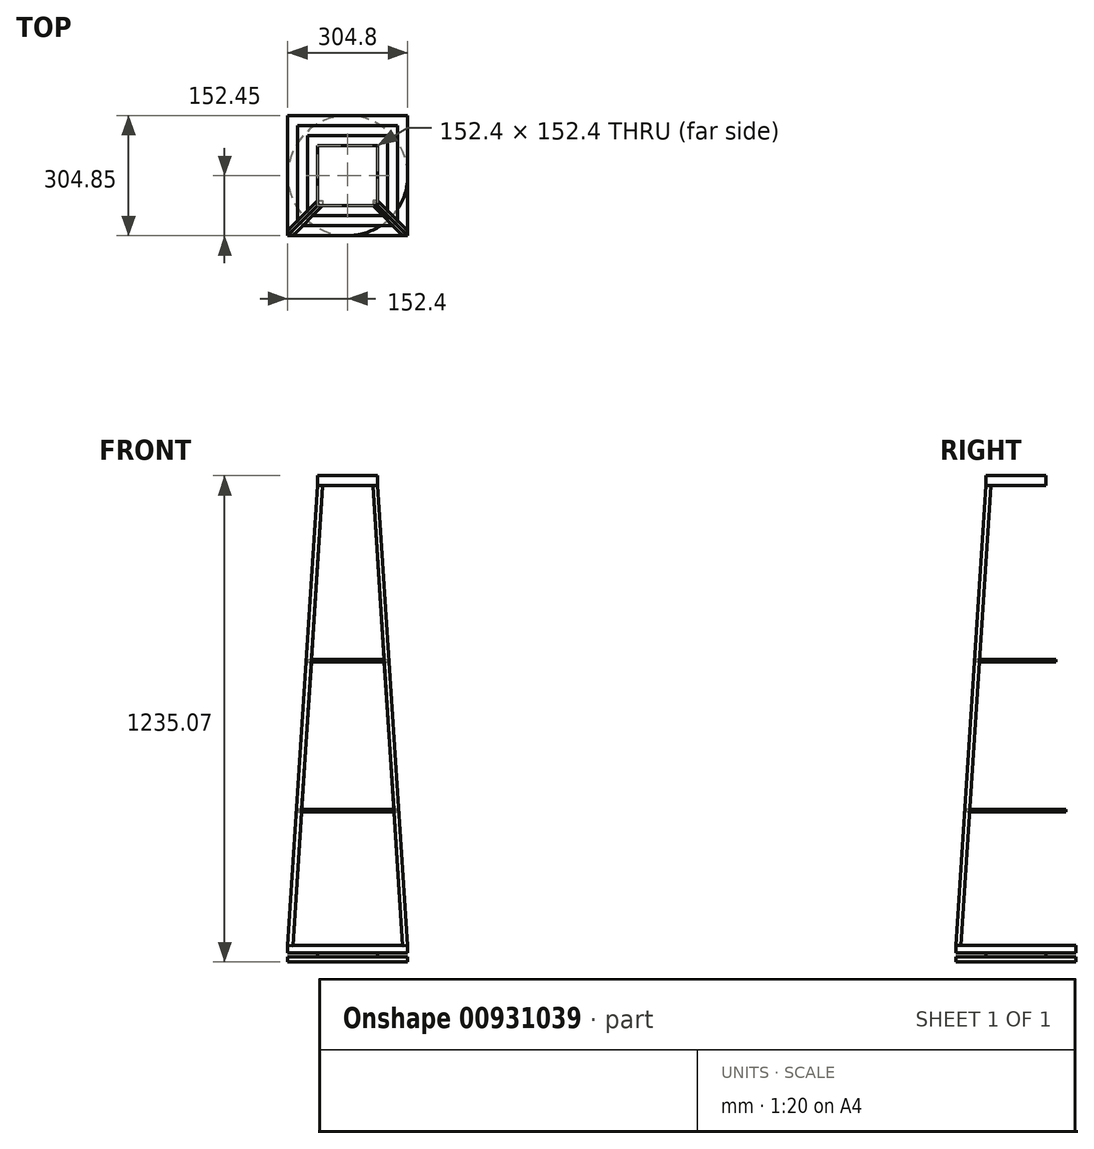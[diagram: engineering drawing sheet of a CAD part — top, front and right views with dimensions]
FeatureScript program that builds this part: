
annotation { "Feature Type Name" : "Feature", "Feature Type Description" : "" }
export const myFeature = defineFeature(function(context is Context, id is Id, definition is map)
    precondition{}
    {
        {
            var Q0;
            Q0=qCreatedBy(makeId("Top.planeOp"),FACE);
            var sketch = newSketch(context, id + "F0", { "sketchPlane" : qUnion([Q0])});
            skCircle(sketch, "E0", {"center": v(0, 0) * mm, "radius": 152.4 * mm});
            skSolve(sketch);
        }
        {
            var Q0;
            Q0 = qSketchRegion(id + "F0", true);
            extrude(context, id + "F1", {"entities" : qUnion([Q0]), "depth" : 12.7 * mm, "offsetDistance" : 25.4 * mm});
        }
        {
            var Q0;
            Q0=makeQuery(id+"F1.opExtrude","CAP_FACE",FACE,{"disambiguationData":[OSD([sQuery(id+"F0.wireOp",EDGE,"E0")])],"isStart":false});
            var sketch = newSketch(context, id + "F2", { "sketchPlane" : qUnion([Q0])});
            skLineSegment(sketch, "E1.bottom", {"start": v(76.2, 76.2) * mm, "end": v(-76.2, 76.2) * mm});
            skLineSegment(sketch, "E1.top", {"start": v(76.2, -76.2) * mm, "end": v(-76.2, -76.2) * mm});
            skLineSegment(sketch, "E1.left", {"start": v(76.2, 76.2) * mm, "end": v(76.2, -76.2) * mm});
            skLineSegment(sketch, "E1.right", {"start": v(-76.2, 76.2) * mm, "end": v(-76.2, -76.2) * mm});
            skPoint(sketch, "E1.middle", {"position": v(0, 0) * mm});
            skSolve(sketch);
        }
        {
            var Q0;
            Q0 = qSketchRegion(id + "F2", true);
            extrude(context, id + "F3", {"entities" : qUnion([Q0]), "operationType" : NewBodyOperationType.ADD, "depth" : 9.52 * mm, "offsetDistance" : 25.4 * mm});
        }
        {
            var Q0;
            Q0=makeQuery(id+"F3.opExtrude","CAP_FACE",FACE,{"disambiguationData":[OSD([sQuery(id+"F2.wireOp",EDGE,"E1.bottom"),sQuery(id+"F2.wireOp",EDGE,"E1.top"),sQuery(id+"F2.wireOp",EDGE,"E1.left"),sQuery(id+"F2.wireOp",EDGE,"E1.right")])],"isStart":false});
            var sketch = newSketch(context, id + "F4", { "sketchPlane" : qUnion([Q0])});
            skLineSegment(sketch, "E2.bottom", {"start": v(152.4, -152.4) * mm, "end": v(-152.4, -152.4) * mm});
            skLineSegment(sketch, "E2.top", {"start": v(152.4, 152.4) * mm, "end": v(-152.4, 152.4) * mm});
            skLineSegment(sketch, "E2.left", {"start": v(152.4, -152.4) * mm, "end": v(152.4, 152.4) * mm});
            skLineSegment(sketch, "E2.right", {"start": v(-152.4, -152.4) * mm, "end": v(-152.4, 152.4) * mm});
            skPoint(sketch, "E2.middle", {"position": v(0, 0) * mm});
            skSolve(sketch);
        }
        {
            var Q0;
            Q0 = qSketchRegion(id + "F4", true);
            extrude(context, id + "F5", {"entities" : qUnion([Q0]), "operationType" : NewBodyOperationType.ADD, "depth" : 19.05 * mm, "offsetDistance" : 25.4 * mm});
        }
        {
            var Q0;
            Q0=makeQuery(id+"F5.opExtrude","CAP_FACE",FACE,{"disambiguationData":[OSD([sQuery(id+"F4.wireOp",EDGE,"E2.bottom"),sQuery(id+"F4.wireOp",EDGE,"E2.top"),sQuery(id+"F4.wireOp",EDGE,"E2.left"),sQuery(id+"F4.wireOp",EDGE,"E2.right")])],"isStart":false});
            cPlane(context, id + "F6", {"entities" : qUnion([Q0]), "cplaneType" : CPlaneType.OFFSET, "offset" : 1168.4 * mm, "width" : 152.4 * mm, "height" : 152.4 * mm});
        }
        {
            var Q0;
            Q0=qCreatedBy(id+"F6.planeOp",FACE);
            var sketch = newSketch(context, id + "F7", { "sketchPlane" : qUnion([Q0])});
            skLineSegment(sketch, "E3.bottom", {"start": v(76.2, -76.2) * mm, "end": v(-76.2, -76.2) * mm});
            skLineSegment(sketch, "E3.top", {"start": v(76.2, 76.2) * mm, "end": v(-76.2, 76.2) * mm});
            skLineSegment(sketch, "E3.left", {"start": v(76.2, -76.2) * mm, "end": v(76.2, 76.2) * mm});
            skLineSegment(sketch, "E3.right", {"start": v(-76.2, -76.2) * mm, "end": v(-76.2, 76.2) * mm});
            skPoint(sketch, "E3.middle", {"position": v(0, 0) * mm});
            skSolve(sketch);
        }
        {
            var Q0;
            Q0 = qSketchRegion(id + "F7", true);
            extrude(context, id + "F8", {"entities" : qUnion([Q0]), "depth" : 25.4 * mm, "offsetDistance" : 25.4 * mm});
        }
        {
            var Q0;
            Q0=makeQuery(id+"F5.opExtrude","CAP_VERTEX",VERTEX,{"disambiguationData":[OSD([sQuery(id+"F4.wireOp",EDGE,"E2.bottom"),sQuery(id+"F4.wireOp",EDGE,"E2.right")])],"isStart":false});
            var Q1;
            Q1=makeQuery(id+"F5.opExtrude","CAP_VERTEX",VERTEX,{"disambiguationData":[OSD([sQuery(id+"F4.wireOp",EDGE,"E2.bottom"),sQuery(id+"F4.wireOp",EDGE,"E2.left")])],"isStart":false});
            var Q2;
            Q2=makeQuery(id+"F8.opExtrude","CAP_VERTEX",VERTEX,{"disambiguationData":[OSD([sQuery(id+"F7.wireOp",EDGE,"E3.bottom"),sQuery(id+"F7.wireOp",EDGE,"E3.right")])],"isStart":true});
            cPlane(context, id + "F9", {"entities" : qUnion([Q0, Q1, Q2]), "cplaneType" : CPlaneType.THREE_POINT, "offset" : 25.4 * mm, "width" : 152.4 * mm, "height" : 152.4 * mm});
        }
        {
            var Q0;
            Q0=qCreatedBy(id+"F9.planeOp",FACE);
            var sketch = newSketch(context, id + "F10", { "sketchPlane" : qUnion([Q0])});
            skPoint(sketch, "E4.0", {"position": v(76.2, 1202.15) * mm});
            skPoint(sketch, "E5.0", {"position": v(-76.2, 1202.15) * mm});
            skPoint(sketch, "E6.0", {"position": v(152.4, 31.27) * mm});
            skPoint(sketch, "E7.0", {"position": v(-152.4, 31.27) * mm});
            skLineSegment(sketch, "E8", {"start": v(76.2, 1202.15) * mm, "end": v(152.4, 31.27) * mm});
            skLineSegment(sketch, "E9", {"start": v(-76.2, 1202.15) * mm, "end": v(-152.4, 31.27) * mm});
            skLineSegment(sketch, "E10", {"start": v(76.2, 1202.15) * mm, "end": v(63.53, 1201.33) * mm});
            skLineSegment(sketch, "E11", {"start": v(-76.2, 1202.15) * mm, "end": v(-63.53, 1201.33) * mm});
            skLineSegment(sketch, "E12", {"start": v(152.4, 31.27) * mm, "end": v(139.73, 30.44) * mm});
            skLineSegment(sketch, "E13", {"start": v(-152.4, 31.27) * mm, "end": v(-139.73, 30.44) * mm});
            skLineSegment(sketch, "E14", {"start": v(139.73, 30.44) * mm, "end": v(63.53, 1201.33) * mm});
            skLineSegment(sketch, "E15", {"start": v(-63.53, 1201.33) * mm, "end": v(-139.73, 30.44) * mm});
            skSolve(sketch);
        }
        {
            var Q0;
            Q0 = qSketchRegion(id + "F10", true);
            extrude(context, id + "F11", {"entities" : qUnion([Q0]), "operationType" : NewBodyOperationType.ADD, "depth" : 12.7 * mm, "offsetDistance" : 25.4 * mm});
        }
        {
            var Q0;
            Q0=qCreatedBy(makeId("Top.planeOp"),FACE);
            cPlane(context, id + "F12", {"entities" : qUnion([Q0]), "cplaneType" : CPlaneType.OFFSET, "offset" : 381 * mm, "width" : 152.4 * mm, "height" : 152.4 * mm});
        }
        {
            var Q0;
            Q0=qCreatedBy(id+"F12.planeOp",FACE);
            var sketch = newSketch(context, id + "F13", { "sketchPlane" : qUnion([Q0])});
            skLineSegment(sketch, "E16.bottom", {"start": v(127, 127) * mm, "end": v(-127, 127) * mm});
            skLineSegment(sketch, "E16.top", {"start": v(127, -127) * mm, "end": v(-127, -127) * mm});
            skLineSegment(sketch, "E16.left", {"start": v(127, 127) * mm, "end": v(127, -127) * mm});
            skLineSegment(sketch, "E16.right", {"start": v(-127, 127) * mm, "end": v(-127, -127) * mm});
            skPoint(sketch, "E16.middle", {"position": v(0, 0) * mm});
            skSolve(sketch);
        }
        {
            var Q0;
            Q0 = qSketchRegion(id + "F13", true);
            extrude(context, id + "F14", {"entities" : qUnion([Q0]), "operationType" : NewBodyOperationType.ADD, "depth" : 6.35 * mm, "offsetDistance" : 25.4 * mm});
        }
        {
            var Q0;
            Q0=qCreatedBy(makeId("Top.planeOp"),FACE);
            cPlane(context, id + "F15", {"entities" : qUnion([Q0]), "cplaneType" : CPlaneType.OFFSET, "offset" : 762 * mm, "width" : 152.4 * mm, "height" : 152.4 * mm});
        }
        {
            var Q0;
            Q0=qCreatedBy(id+"F15.planeOp",FACE);
            var sketch = newSketch(context, id + "F16", { "sketchPlane" : qUnion([Q0])});
            skLineSegment(sketch, "E17.bottom", {"start": v(-101.6, 101.6) * mm, "end": v(101.6, 101.6) * mm});
            skLineSegment(sketch, "E17.top", {"start": v(-101.6, -101.6) * mm, "end": v(101.6, -101.6) * mm});
            skLineSegment(sketch, "E17.left", {"start": v(-101.6, 101.6) * mm, "end": v(-101.6, -101.6) * mm});
            skLineSegment(sketch, "E17.right", {"start": v(101.6, 101.6) * mm, "end": v(101.6, -101.6) * mm});
            skPoint(sketch, "E17.middle", {"position": v(0, 0) * mm});
            skSolve(sketch);
        }
        {
            var Q0;
            Q0 = qSketchRegion(id + "F16", true);
            extrude(context, id + "F17", {"entities" : qUnion([Q0]), "operationType" : NewBodyOperationType.ADD, "depth" : 6.35 * mm, "offsetDistance" : 25.4 * mm});
        }
    });
